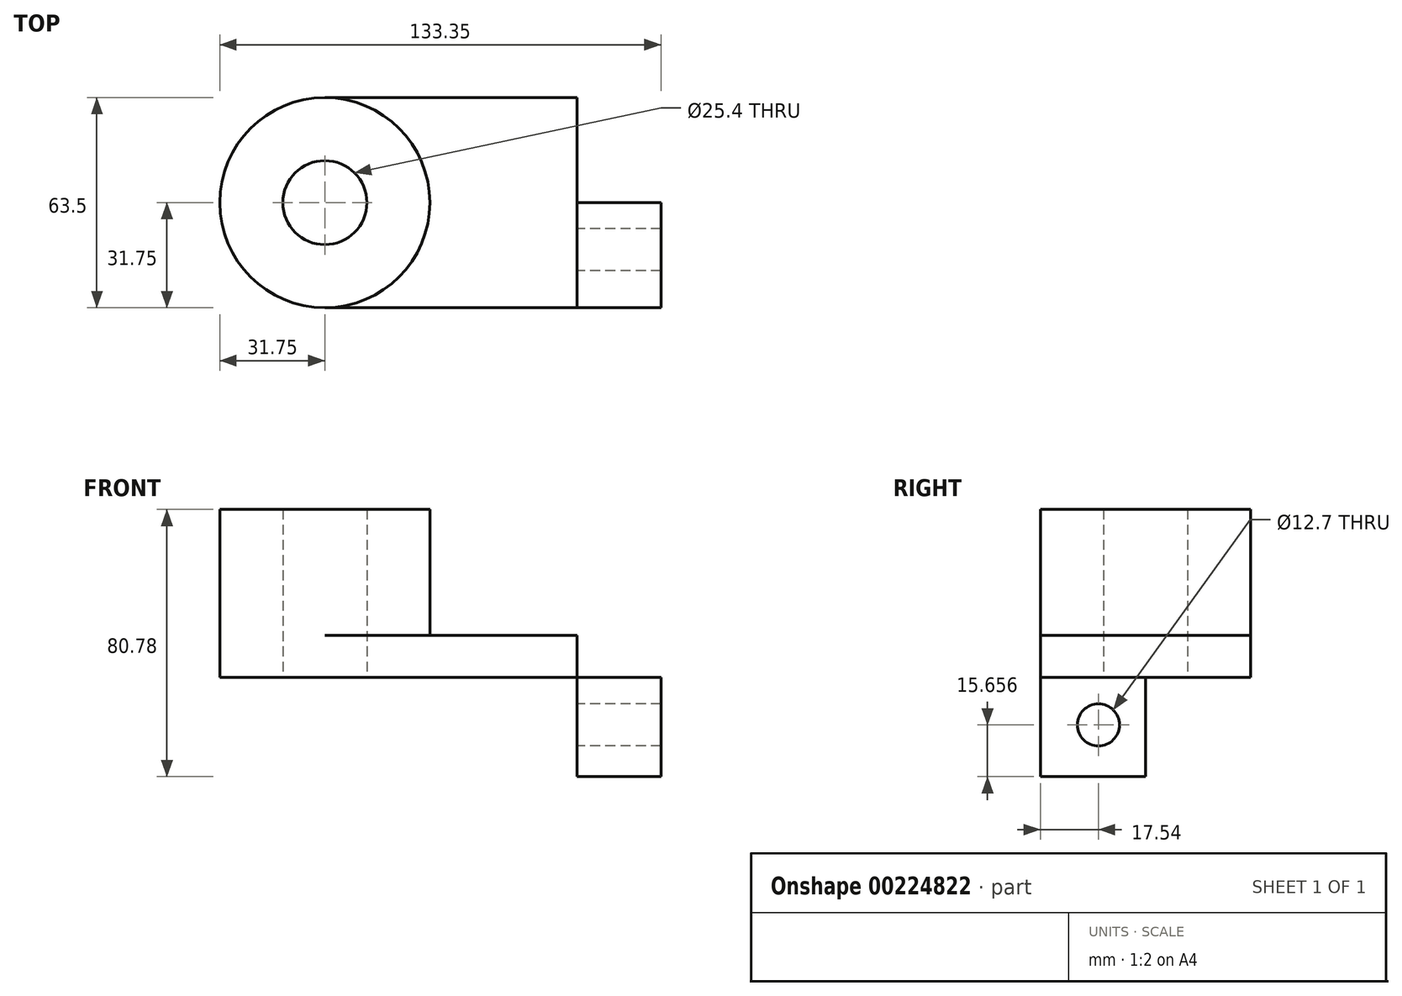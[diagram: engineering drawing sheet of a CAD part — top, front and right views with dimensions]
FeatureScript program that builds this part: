
annotation { "Feature Type Name" : "Feature", "Feature Type Description" : "" }
export const myFeature = defineFeature(function(context is Context, id is Id, definition is map)
    precondition{}
    {
        {
            var Q0;
            Q0=qCreatedBy(makeId("Top.planeOp"),FACE);
            var sketch = newSketch(context, id + "F0", { "sketchPlane" : qUnion([Q0])});
            skLineSegment(sketch, "E0.bottom", {"start": v(-38.1, 31.75) * mm, "end": v(38.1, 31.75) * mm});
            skLineSegment(sketch, "E0.top", {"start": v(-38.1, -31.75) * mm, "end": v(38.1, -31.75) * mm});
            skLineSegment(sketch, "E0.left", {"start": v(-38.1, 31.75) * mm, "end": v(-38.1, -31.75) * mm});
            skLineSegment(sketch, "E0.right", {"start": v(38.1, 31.75) * mm, "end": v(38.1, -31.75) * mm});
            skPoint(sketch, "E0.middle", {"position": v(0, 0) * mm});
            skCircle(sketch, "E1", {"center": v(-38.1, 0) * mm, "radius": 31.75 * mm});
            skCircle(sketch, "E2", {"center": v(-38.1, 0) * mm, "radius": 12.7 * mm});
            skSolve(sketch);
        }
        {
            var Q0;
            Q0=qSketchRegion(id+"F0",true);
            extrude(context, id + "F1", {"entities" : qUnion([Q0]), "depth" : 12.7 * mm});
        }
        {
            var Q0;
            {var subQ1=sQuery(id+"F0.wireOp",EDGE,"E0.left");var subQ3=sQuery(id+"F0.wireOp",EDGE,"E2");var subQ4=makeQuery(id+"F0.imprint","INTERSECT",VERTEX,{"disambiguationData":[OD(0.0)],"derivedFrom":[subQ1,subQ3]});Q0=makeQuery(id+"F0.imprint","IMPRINT",FACE,{"disambiguationData":[TD([[makeQuery(id+"F0.imprint","IMPRINT",EDGE,{"disambiguationData":[TD([[subQ4,-1.0]])],"derivedFrom":subQ3}),-1.0]])]});}
            extrude(context, id + "F2", {"entities" : qUnion([Q0]), "operationType" : NewBodyOperationType.ADD, "depth" : 50.8 * mm});
        }
        {
            var Q0;
            {var subQ1=sQuery(id+"F0.wireOp",EDGE,"E0.left");var subQ3=sQuery(id+"F0.wireOp",EDGE,"E2");var subQ4=makeQuery(id+"F0.imprint","INTERSECT",VERTEX,{"disambiguationData":[OD(0.0)],"derivedFrom":[subQ1,subQ3]});Q0=makeQuery(id+"F0.imprint","IMPRINT",FACE,{"disambiguationData":[TD([[makeQuery(id+"F0.imprint","IMPRINT",EDGE,{"disambiguationData":[TD([[subQ4,1.0]])],"derivedFrom":subQ3}),-1.0]])]});}
            extrude(context, id + "F3", {"entities" : qUnion([Q0]), "operationType" : NewBodyOperationType.ADD, "depth" : 50.8 * mm});
        }
        {
            var Q0;
            Q0=makeQuery(id+"F1.opExtrude","SWEPT_FACE",FACE,{"disambiguationData":[OSD([sQuery(id+"F0.wireOp",EDGE,"E0.right")])]});
            var sketch = newSketch(context, id + "F4", { "sketchPlane" : qUnion([Q0])});
            skLineSegment(sketch, "E3.bottom", {"start": v(-31.75, 12.7) * mm, "end": v(31.98, 12.7) * mm});
            skLineSegment(sketch, "E3.top", {"start": v(-31.75, -29.98) * mm, "end": v(31.98, -29.98) * mm});
            skLineSegment(sketch, "E3.left", {"start": v(-31.75, 12.7) * mm, "end": v(-31.75, -29.98) * mm});
            skLineSegment(sketch, "E3.right", {"start": v(31.98, 12.7) * mm, "end": v(31.98, -29.98) * mm});
            skCircle(sketch, "E4", {"center": v(-14.21, -14.32) * mm, "radius": 6.35 * mm});
            skLineSegment(sketch, "E5", {"start": v(0, 0) * mm, "end": v(0, -29.98) * mm});
            skCircle(sketch, "E6.MirrorC", {"center": v(14.21, -14.32) * mm, "radius": 6.35 * mm});
            skSolve(sketch);
        }
        {
            var Q0;
            Q0=makeQuery(id+"F4.imprint","IMPRINT",FACE,{"disambiguationData":[TD([[makeQuery(id+"F4.imprint","IMPRINT",EDGE,{"derivedFrom":sQuery(id+"F4.wireOp",EDGE,"E4")}),-1.0]])]});
            extrude(context, id + "F5", {"entities" : qUnion([Q0]), "depth" : 25.4 * mm});
        }
    });
